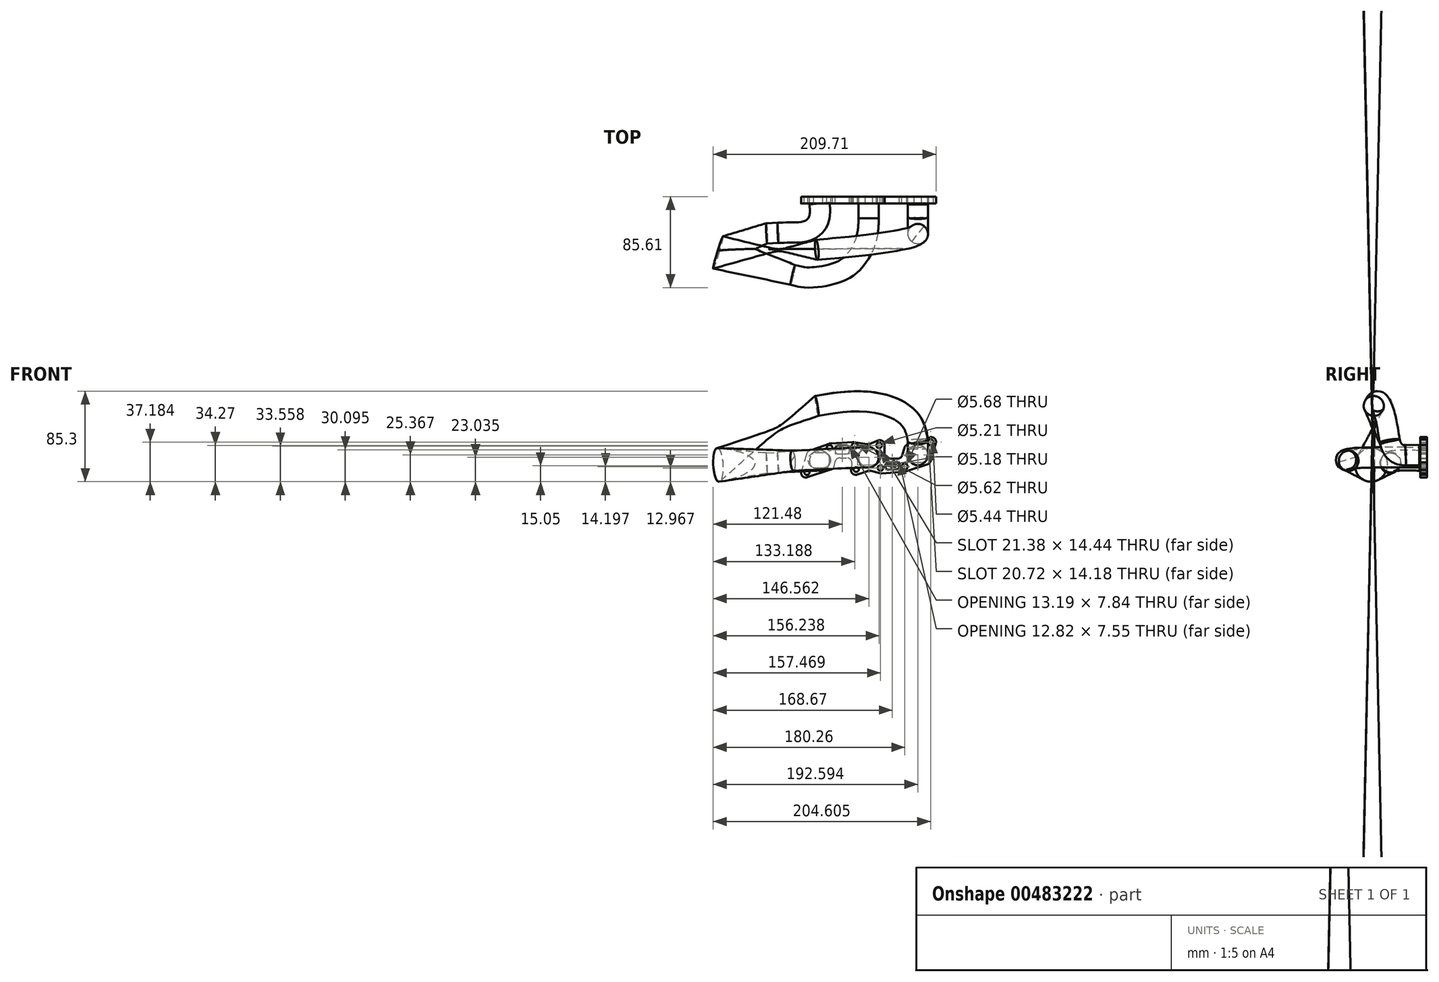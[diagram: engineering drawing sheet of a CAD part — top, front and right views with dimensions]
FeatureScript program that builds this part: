
annotation { "Feature Type Name" : "Feature", "Feature Type Description" : "" }
export const myFeature = defineFeature(function(context is Context, id is Id, definition is map)
    precondition{}
    {
        {
            var Q0;
            Q0=qCreatedBy(makeId("Front.planeOp"),FACE);
            var sketch = newSketch(context, id + "F0", { "sketchPlane" : qUnion([Q0])});
            skLineSegment(sketch, "E0", {"start": v(-73.48, -2.45) * mm, "end": v(-78.33, -18.68) * mm});
            skLineSegment(sketch, "E1", {"start": v(-72.7, -24.18) * mm, "end": v(-50.65, -16.95) * mm});
            skLineSegment(sketch, "E2", {"start": v(-47.2, -12.82) * mm, "end": v(-46.84, -10.23) * mm});
            skLineSegment(sketch, "E3", {"start": v(-41.8, -5.85) * mm, "end": v(-35.77, -5.85) * mm});
            skLineSegment(sketch, "E4", {"start": v(-30.75, -11.68) * mm, "end": v(-31.51, -16.81) * mm});
            skLineSegment(sketch, "E5", {"start": v(-25.64, -21.66) * mm, "end": v(-16.08, -18.29) * mm});
            skLineSegment(sketch, "E6", {"start": v(-13.09, -18.17) * mm, "end": v(-4.67, -20.4) * mm});
            skLineSegment(sketch, "E7", {"start": v(-3, -20.56) * mm, "end": v(18.71, -18.98) * mm});
            skLineSegment(sketch, "E8", {"start": v(19.92, -18.74) * mm, "end": v(40.2, -12.13) * mm});
            skLineSegment(sketch, "E9", {"start": v(43.5, -8.7) * mm, "end": v(48.23, 7.92) * mm});
            skLineSegment(sketch, "E10", {"start": v(42.6, 13.37) * mm, "end": v(21.88, 6.74) * mm});
            skLineSegment(sketch, "E11", {"start": v(18.52, 3.22) * mm, "end": v(16.86, -2.97) * mm});
            skLineSegment(sketch, "E12", {"start": v(11.95, -6.74) * mm, "end": v(5.08, -6.74) * mm});
            skLineSegment(sketch, "E13", {"start": v(0, -1.66) * mm, "end": v(0, 6.27) * mm});
            skLineSegment(sketch, "E14", {"start": v(-6.09, 10.4) * mm, "end": v(-13.83, 7.32) * mm});
            skLineSegment(sketch, "E15", {"start": v(-16.46, 7.02) * mm, "end": v(-28.88, 8.87) * mm});
            skLineSegment(sketch, "E16", {"start": v(-29.9, 8.92) * mm, "end": v(-50.7, 7.78) * mm});
            skLineSegment(sketch, "E17", {"start": v(-52.15, 7.48) * mm, "end": v(-70.34, 0.87) * mm});
            skLineSegment(sketch, "E18", {"start": v(-64.86, -0.9) * mm, "end": v(-57.65, -0.9) * mm});
            skLineSegment(sketch, "E19", {"start": v(-66.6, -15.1) * mm, "end": v(-58.23, -15.1) * mm});
            skArc(sketch, "E20", {"start": v(-64.86, -0.9) * mm, "mid": v(-72, -7.23) * mm, "end": v(-66.6, -15.1) * mm});
            skArc(sketch, "E21", {"start": v(-57.65, -0.9) * mm, "mid": v(-50.55, -8.3) * mm, "end": v(-58.23, -15.1) * mm});
            skLineSegment(sketch, "E22", {"start": v(-43.8, -2.2) * mm, "end": v(-35.78, -2.2) * mm});
            skLineSegment(sketch, "E23", {"start": v(-33.24, 0.34) * mm, "end": v(-33.24, 3.1) * mm});
            skLineSegment(sketch, "E24", {"start": v(-35.78, 5.63) * mm, "end": v(-43.88, 5.63) * mm});
            skLineSegment(sketch, "E25", {"start": v(-46.42, 3) * mm, "end": v(-46.33, 0.25) * mm});
            skLineSegment(sketch, "E26", {"start": v(-18.09, -12.57) * mm, "end": v(-11.17, -12.34) * mm});
            skLineSegment(sketch, "E27", {"start": v(-18.22, 1.88) * mm, "end": v(-11.17, 1.88) * mm});
            skArc(sketch, "E28", {"start": v(-18.22, 1.88) * mm, "mid": v(-25.44, -5.4) * mm, "end": v(-18.09, -12.57) * mm});
            skArc(sketch, "E29", {"start": v(-11.17, 1.88) * mm, "mid": v(-4.06, -5.23) * mm, "end": v(-11.17, -12.34) * mm});
            skLineSegment(sketch, "E30", {"start": v(27.76, -10.1) * mm, "end": v(34.68, -10.1) * mm});
            skLineSegment(sketch, "E31", {"start": v(28.01, 4.08) * mm, "end": v(34.55, 4.08) * mm});
            skArc(sketch, "E32", {"start": v(28.01, 4.08) * mm, "mid": v(20.92, -2.89) * mm, "end": v(27.76, -10.1) * mm});
            skArc(sketch, "E33", {"start": v(34.55, 4.08) * mm, "mid": v(41.64, -2.95) * mm, "end": v(34.68, -10.1) * mm});
            skLineSegment(sketch, "E34", {"start": v(3.6, -17.1) * mm, "end": v(11.35, -16.75) * mm});
            skLineSegment(sketch, "E35", {"start": v(13.77, -14.22) * mm, "end": v(13.77, -12.09) * mm});
            skLineSegment(sketch, "E36", {"start": v(11.08, -9.55) * mm, "end": v(3.34, -10.02) * mm});
            skLineSegment(sketch, "E37", {"start": v(0.95, -12.56) * mm, "end": v(0.95, -14.57) * mm});
            skCircle(sketch, "E38", {"center": v(-73.06, -19.56) * mm, "radius": 2.44 * mm});
            skCircle(sketch, "E39", {"center": v(-51.69, 3.62) * mm, "radius": 2.58 * mm});
            skCircle(sketch, "E40", {"center": v(-28.12, 5.18) * mm, "radius": 2.8 * mm});
            skCircle(sketch, "E41", {"center": v(-26.7, -16.7) * mm, "radius": 2.47 * mm});
            skCircle(sketch, "E42", {"center": v(-3.84, -15.41) * mm, "radius": 2.6 * mm});
            skCircle(sketch, "E43", {"center": v(-5.07, 5.9) * mm, "radius": 2.6 * mm});
            skCircle(sketch, "E44", {"center": v(18.95, -14.18) * mm, "radius": 2.84 * mm});
            skCircle(sketch, "E45", {"center": v(43.3, 8.8) * mm, "radius": 2.72 * mm});
            skPoint(sketch, "E46.visualSharp", {"position": v(50.5, 15.9) * mm});
            skArc(sketch, "E46.filletArc", {"start": v(48.23, 7.92) * mm, "mid": v(47.05, 12.33) * mm, "end": v(42.6, 13.37) * mm});
            skPoint(sketch, "E47.visualSharp", {"position": v(0, 12.82) * mm});
            skArc(sketch, "E47.filletArc", {"start": v(0, 6.27) * mm, "mid": v(-1.95, 9.95) * mm, "end": v(-6.09, 10.4) * mm});
            skPoint(sketch, "E48.visualSharp", {"position": v(-32.6, -24.11) * mm});
            skArc(sketch, "E48.filletArc", {"start": v(-31.51, -16.81) * mm, "mid": v(-29.95, -20.9) * mm, "end": v(-25.64, -21.66) * mm});
            skPoint(sketch, "E49.visualSharp", {"position": v(-80.77, -26.83) * mm});
            skArc(sketch, "E49.filletArc", {"start": v(-78.33, -18.68) * mm, "mid": v(-77.18, -23.14) * mm, "end": v(-72.7, -24.18) * mm});
            skPoint(sketch, "E50.visualSharp", {"position": v(-47.63, -15.96) * mm});
            skArc(sketch, "E50.filletArc", {"start": v(-50.65, -16.95) * mm, "mid": v(-48.33, -15.38) * mm, "end": v(-47.2, -12.82) * mm});
            skPoint(sketch, "E51.visualSharp", {"position": v(-46.23, -5.85) * mm});
            skArc(sketch, "E51.filletArc", {"start": v(-41.8, -5.85) * mm, "mid": v(-45.14, -7.1) * mm, "end": v(-46.84, -10.23) * mm});
            skPoint(sketch, "E52.visualSharp", {"position": v(-29.88, -5.85) * mm});
            skArc(sketch, "E52.filletArc", {"start": v(-30.75, -11.68) * mm, "mid": v(-31.93, -7.62) * mm, "end": v(-35.77, -5.85) * mm});
            skPoint(sketch, "E53.visualSharp", {"position": v(-14.6, -17.77) * mm});
            skArc(sketch, "E53.filletArc", {"start": v(-13.09, -18.17) * mm, "mid": v(-14.6, -18) * mm, "end": v(-16.08, -18.29) * mm});
            skPoint(sketch, "E54.visualSharp", {"position": v(-3.85, -20.62) * mm});
            skArc(sketch, "E54.filletArc", {"start": v(-4.67, -20.4) * mm, "mid": v(-3.84, -20.55) * mm, "end": v(-3, -20.56) * mm});
            skPoint(sketch, "E55.visualSharp", {"position": v(19.33, -18.93) * mm});
            skArc(sketch, "E55.filletArc", {"start": v(18.71, -18.98) * mm, "mid": v(19.32, -18.9) * mm, "end": v(19.92, -18.74) * mm});
            skPoint(sketch, "E56.visualSharp", {"position": v(42.77, -11.3) * mm});
            skArc(sketch, "E56.filletArc", {"start": v(40.2, -12.13) * mm, "mid": v(42.28, -10.83) * mm, "end": v(43.5, -8.7) * mm});
            skPoint(sketch, "E57.visualSharp", {"position": v(19.24, 5.9) * mm});
            skArc(sketch, "E57.filletArc", {"start": v(21.88, 6.74) * mm, "mid": v(19.75, 5.4) * mm, "end": v(18.52, 3.22) * mm});
            skPoint(sketch, "E58.visualSharp", {"position": v(15.85, -6.74) * mm});
            skArc(sketch, "E58.filletArc", {"start": v(11.95, -6.74) * mm, "mid": v(15.05, -5.69) * mm, "end": v(16.86, -2.97) * mm});
            skPoint(sketch, "E59.visualSharp", {"position": v(0, -6.74) * mm});
            skArc(sketch, "E59.filletArc", {"start": v(0, -1.66) * mm, "mid": v(1.49, -5.25) * mm, "end": v(5.08, -6.74) * mm});
            skPoint(sketch, "E60.visualSharp", {"position": v(-72.74, 0) * mm});
            skArc(sketch, "E60.filletArc", {"start": v(-70.34, 0.87) * mm, "mid": v(-72.3, -0.42) * mm, "end": v(-73.48, -2.45) * mm});
            skPoint(sketch, "E61.visualSharp", {"position": v(-51.44, 7.74) * mm});
            skArc(sketch, "E61.filletArc", {"start": v(-50.7, 7.78) * mm, "mid": v(-51.43, 7.69) * mm, "end": v(-52.15, 7.48) * mm});
            skPoint(sketch, "E62.visualSharp", {"position": v(-29.39, 8.94) * mm});
            skArc(sketch, "E62.filletArc", {"start": v(-28.88, 8.87) * mm, "mid": v(-29.39, 8.92) * mm, "end": v(-29.9, 8.92) * mm});
            skPoint(sketch, "E63.visualSharp", {"position": v(-15.1, 6.82) * mm});
            skArc(sketch, "E63.filletArc", {"start": v(-16.46, 7.02) * mm, "mid": v(-15.12, 7) * mm, "end": v(-13.83, 7.32) * mm});
            skPoint(sketch, "E64.visualSharp", {"position": v(-46.25, -2.2) * mm});
            skArc(sketch, "E64.filletArc", {"start": v(-46.33, 0.25) * mm, "mid": v(-45.56, -1.49) * mm, "end": v(-43.8, -2.2) * mm});
            skPoint(sketch, "E65.visualSharp", {"position": v(-33.24, -2.2) * mm});
            skArc(sketch, "E65.filletArc", {"start": v(-35.78, -2.2) * mm, "mid": v(-33.98, -1.46) * mm, "end": v(-33.24, 0.34) * mm});
            skPoint(sketch, "E66.visualSharp", {"position": v(-33.24, 5.63) * mm});
            skArc(sketch, "E66.filletArc", {"start": v(-33.24, 3.1) * mm, "mid": v(-33.98, 4.89) * mm, "end": v(-35.78, 5.63) * mm});
            skPoint(sketch, "E67.visualSharp", {"position": v(-46.51, 5.63) * mm});
            skArc(sketch, "E67.filletArc", {"start": v(-43.88, 5.63) * mm, "mid": v(-45.71, 4.86) * mm, "end": v(-46.42, 3) * mm});
            skPoint(sketch, "E68.visualSharp", {"position": v(0.95, -10.17) * mm});
            skArc(sketch, "E68.filletArc", {"start": v(3.34, -10.02) * mm, "mid": v(1.64, -10.82) * mm, "end": v(0.95, -12.56) * mm});
            skPoint(sketch, "E69.visualSharp", {"position": v(13.77, -9.4) * mm});
            skArc(sketch, "E69.filletArc", {"start": v(13.77, -12.09) * mm, "mid": v(12.97, -10.24) * mm, "end": v(11.08, -9.55) * mm});
            skPoint(sketch, "E70.visualSharp", {"position": v(13.77, -16.64) * mm});
            skArc(sketch, "E70.filletArc", {"start": v(11.35, -16.75) * mm, "mid": v(13.07, -15.97) * mm, "end": v(13.77, -14.22) * mm});
            skPoint(sketch, "E71.visualSharp", {"position": v(0.95, -17.23) * mm});
            skArc(sketch, "E71.filletArc", {"start": v(0.95, -14.57) * mm, "mid": v(1.73, -16.4) * mm, "end": v(3.6, -17.1) * mm});
            skPoint(sketch, "E72", {"position": v(-61.27, -8.01) * mm});
            skPoint(sketch, "E73", {"position": v(-14.89, -5.4) * mm});
            skPoint(sketch, "E73.positionSnap0", {"position": v(-25.44, -5.4) * mm});
            skPoint(sketch, "E74", {"position": v(31.4, -3.13) * mm});
            skSolve(sketch);
        }
        {
            var Q0;
            Q0=makeQuery(id+"F0.imprint","IMPRINT",FACE,{"disambiguationData":[TD([[makeQuery(id+"F0.imprint","IMPRINT",EDGE,{"derivedFrom":sQuery(id+"F0.wireOp",EDGE,"E0")}),1.0]])]});
            extrude(context, id + "F1", {"entities" : qUnion([Q0]), "depth" : 6.35 * mm});
        }
        {
            var Q0;
            Q0=qCreatedBy(makeId("Right.planeOp"),FACE);
            cPlane(context, id + "F2", {"entities" : qUnion([Q0]), "cplaneType" : CPlaneType.OFFSET, "offset" : 61.2 * mm, "oppositeDirection" : true, "width" : 152.4 * mm, "height" : 152.4 * mm});
        }
        {
            var Q0;
            Q0=qCreatedBy(id+"F2.planeOp",FACE);
            cPlane(context, id + "F3", {"entities" : qUnion([Q0]), "cplaneType" : CPlaneType.OFFSET, "offset" : 46.23 * mm, "width" : 152.4 * mm, "height" : 152.4 * mm});
        }
        {
            var Q0;
            Q0=qCreatedBy(id+"F2.planeOp",FACE);
            cPlane(context, id + "F4", {"entities" : qUnion([Q0]), "cplaneType" : CPlaneType.OFFSET, "offset" : 92.66 * mm, "width" : 152.4 * mm, "height" : 152.4 * mm});
        }
        {
            var Q0;
            Q0=makeQuery(id+"F1.opExtrude","CAP_FACE",FACE,{"disambiguationData":[OSD([sQuery(id+"F0.wireOp",EDGE,"E0"),sQuery(id+"F0.wireOp",EDGE,"E1"),sQuery(id+"F0.wireOp",EDGE,"E2"),sQuery(id+"F0.wireOp",EDGE,"E3"),sQuery(id+"F0.wireOp",EDGE,"E4"),sQuery(id+"F0.wireOp",EDGE,"E5"),sQuery(id+"F0.wireOp",EDGE,"E6"),sQuery(id+"F0.wireOp",EDGE,"E7"),sQuery(id+"F0.wireOp",EDGE,"E8"),sQuery(id+"F0.wireOp",EDGE,"E9"),sQuery(id+"F0.wireOp",EDGE,"E10"),sQuery(id+"F0.wireOp",EDGE,"E11"),sQuery(id+"F0.wireOp",EDGE,"E12"),sQuery(id+"F0.wireOp",EDGE,"E13"),sQuery(id+"F0.wireOp",EDGE,"E14"),sQuery(id+"F0.wireOp",EDGE,"E15"),sQuery(id+"F0.wireOp",EDGE,"E16"),sQuery(id+"F0.wireOp",EDGE,"E17"),sQuery(id+"F0.wireOp",EDGE,"E18"),sQuery(id+"F0.wireOp",EDGE,"E19"),sQuery(id+"F0.wireOp",EDGE,"E20"),sQuery(id+"F0.wireOp",EDGE,"E21"),sQuery(id+"F0.wireOp",EDGE,"E22"),sQuery(id+"F0.wireOp",EDGE,"E23"),sQuery(id+"F0.wireOp",EDGE,"E24"),sQuery(id+"F0.wireOp",EDGE,"E25"),sQuery(id+"F0.wireOp",EDGE,"E26"),sQuery(id+"F0.wireOp",EDGE,"E27"),sQuery(id+"F0.wireOp",EDGE,"E28"),sQuery(id+"F0.wireOp",EDGE,"E29"),sQuery(id+"F0.wireOp",EDGE,"E30"),sQuery(id+"F0.wireOp",EDGE,"E31"),sQuery(id+"F0.wireOp",EDGE,"E32"),sQuery(id+"F0.wireOp",EDGE,"E33"),sQuery(id+"F0.wireOp",EDGE,"E34"),sQuery(id+"F0.wireOp",EDGE,"E35"),sQuery(id+"F0.wireOp",EDGE,"E36"),sQuery(id+"F0.wireOp",EDGE,"E37"),sQuery(id+"F0.wireOp",EDGE,"E38"),sQuery(id+"F0.wireOp",EDGE,"E39"),sQuery(id+"F0.wireOp",EDGE,"E40"),sQuery(id+"F0.wireOp",EDGE,"E41"),sQuery(id+"F0.wireOp",EDGE,"E42"),sQuery(id+"F0.wireOp",EDGE,"E43"),sQuery(id+"F0.wireOp",EDGE,"E44"),sQuery(id+"F0.wireOp",EDGE,"E45"),sQuery(id+"F0.wireOp",EDGE,"E46.filletArc"),sQuery(id+"F0.wireOp",EDGE,"E47.filletArc"),sQuery(id+"F0.wireOp",EDGE,"E48.filletArc"),sQuery(id+"F0.wireOp",EDGE,"E49.filletArc"),sQuery(id+"F0.wireOp",EDGE,"E50.filletArc"),sQuery(id+"F0.wireOp",EDGE,"E51.filletArc"),sQuery(id+"F0.wireOp",EDGE,"E52.filletArc"),sQuery(id+"F0.wireOp",EDGE,"E53.filletArc"),sQuery(id+"F0.wireOp",EDGE,"E54.filletArc"),sQuery(id+"F0.wireOp",EDGE,"E55.filletArc"),sQuery(id+"F0.wireOp",EDGE,"E56.filletArc"),sQuery(id+"F0.wireOp",EDGE,"E57.filletArc"),sQuery(id+"F0.wireOp",EDGE,"E58.filletArc"),sQuery(id+"F0.wireOp",EDGE,"E59.filletArc"),sQuery(id+"F0.wireOp",EDGE,"E60.filletArc"),sQuery(id+"F0.wireOp",EDGE,"E61.filletArc"),sQuery(id+"F0.wireOp",EDGE,"E62.filletArc"),sQuery(id+"F0.wireOp",EDGE,"E63.filletArc"),sQuery(id+"F0.wireOp",EDGE,"E64.filletArc"),sQuery(id+"F0.wireOp",EDGE,"E65.filletArc"),sQuery(id+"F0.wireOp",EDGE,"E66.filletArc"),sQuery(id+"F0.wireOp",EDGE,"E67.filletArc"),sQuery(id+"F0.wireOp",EDGE,"E68.filletArc"),sQuery(id+"F0.wireOp",EDGE,"E69.filletArc"),sQuery(id+"F0.wireOp",EDGE,"E70.filletArc"),sQuery(id+"F0.wireOp",EDGE,"E71.filletArc")])],"isStart":false});
            cPlane(context, id + "F5", {"entities" : qUnion([Q0]), "cplaneType" : CPlaneType.OFFSET, "offset" : 0 * mm, "width" : 152.4 * mm, "height" : 152.4 * mm});
        }
        {
            var Q0;
            Q0=qCreatedBy(id+"F5.planeOp",FACE);
            var sketch = newSketch(context, id + "F6", { "sketchPlane" : qUnion([Q0])});
            skPoint(sketch, "E75", {"position": v(-61.33, -8.01) * mm});
            skPoint(sketch, "E76", {"position": v(-14.86, -5.46) * mm});
            skPoint(sketch, "E77", {"position": v(31.4, -3.17) * mm});
            skSolve(sketch);
        }
        {
            var Q0;
            Q0=qCreatedBy(id+"F3.planeOp",FACE);
            var sketch = newSketch(context, id + "F7", { "sketchPlane" : qUnion([Q0])});
            skLineSegment(sketch, "E78", {"start": v(-6.35, -5.46) * mm, "end": v(-20.21, -5.46) * mm});
            skPoint(sketch, "E79", {"position": v(-6.35, -5.46) * mm});
            skSolve(sketch);
        }
        {
            var Q0;
            Q0=makeQuery(id+"F1.opExtrude","CAP_FACE",FACE,{"disambiguationData":[OSD([sQuery(id+"F0.wireOp",EDGE,"E0"),sQuery(id+"F0.wireOp",EDGE,"E1"),sQuery(id+"F0.wireOp",EDGE,"E2"),sQuery(id+"F0.wireOp",EDGE,"E3"),sQuery(id+"F0.wireOp",EDGE,"E4"),sQuery(id+"F0.wireOp",EDGE,"E5"),sQuery(id+"F0.wireOp",EDGE,"E6"),sQuery(id+"F0.wireOp",EDGE,"E7"),sQuery(id+"F0.wireOp",EDGE,"E8"),sQuery(id+"F0.wireOp",EDGE,"E9"),sQuery(id+"F0.wireOp",EDGE,"E10"),sQuery(id+"F0.wireOp",EDGE,"E11"),sQuery(id+"F0.wireOp",EDGE,"E12"),sQuery(id+"F0.wireOp",EDGE,"E13"),sQuery(id+"F0.wireOp",EDGE,"E14"),sQuery(id+"F0.wireOp",EDGE,"E15"),sQuery(id+"F0.wireOp",EDGE,"E16"),sQuery(id+"F0.wireOp",EDGE,"E17"),sQuery(id+"F0.wireOp",EDGE,"E18"),sQuery(id+"F0.wireOp",EDGE,"E19"),sQuery(id+"F0.wireOp",EDGE,"E20"),sQuery(id+"F0.wireOp",EDGE,"E21"),sQuery(id+"F0.wireOp",EDGE,"E22"),sQuery(id+"F0.wireOp",EDGE,"E23"),sQuery(id+"F0.wireOp",EDGE,"E24"),sQuery(id+"F0.wireOp",EDGE,"E25"),sQuery(id+"F0.wireOp",EDGE,"E26"),sQuery(id+"F0.wireOp",EDGE,"E27"),sQuery(id+"F0.wireOp",EDGE,"E28"),sQuery(id+"F0.wireOp",EDGE,"E29"),sQuery(id+"F0.wireOp",EDGE,"E30"),sQuery(id+"F0.wireOp",EDGE,"E31"),sQuery(id+"F0.wireOp",EDGE,"E32"),sQuery(id+"F0.wireOp",EDGE,"E33"),sQuery(id+"F0.wireOp",EDGE,"E34"),sQuery(id+"F0.wireOp",EDGE,"E35"),sQuery(id+"F0.wireOp",EDGE,"E36"),sQuery(id+"F0.wireOp",EDGE,"E37"),sQuery(id+"F0.wireOp",EDGE,"E38"),sQuery(id+"F0.wireOp",EDGE,"E39"),sQuery(id+"F0.wireOp",EDGE,"E40"),sQuery(id+"F0.wireOp",EDGE,"E41"),sQuery(id+"F0.wireOp",EDGE,"E42"),sQuery(id+"F0.wireOp",EDGE,"E43"),sQuery(id+"F0.wireOp",EDGE,"E44"),sQuery(id+"F0.wireOp",EDGE,"E45"),sQuery(id+"F0.wireOp",EDGE,"E46.filletArc"),sQuery(id+"F0.wireOp",EDGE,"E47.filletArc"),sQuery(id+"F0.wireOp",EDGE,"E48.filletArc"),sQuery(id+"F0.wireOp",EDGE,"E49.filletArc"),sQuery(id+"F0.wireOp",EDGE,"E50.filletArc"),sQuery(id+"F0.wireOp",EDGE,"E51.filletArc"),sQuery(id+"F0.wireOp",EDGE,"E52.filletArc"),sQuery(id+"F0.wireOp",EDGE,"E53.filletArc"),sQuery(id+"F0.wireOp",EDGE,"E54.filletArc"),sQuery(id+"F0.wireOp",EDGE,"E55.filletArc"),sQuery(id+"F0.wireOp",EDGE,"E56.filletArc"),sQuery(id+"F0.wireOp",EDGE,"E57.filletArc"),sQuery(id+"F0.wireOp",EDGE,"E58.filletArc"),sQuery(id+"F0.wireOp",EDGE,"E59.filletArc"),sQuery(id+"F0.wireOp",EDGE,"E60.filletArc"),sQuery(id+"F0.wireOp",EDGE,"E61.filletArc"),sQuery(id+"F0.wireOp",EDGE,"E62.filletArc"),sQuery(id+"F0.wireOp",EDGE,"E63.filletArc"),sQuery(id+"F0.wireOp",EDGE,"E64.filletArc"),sQuery(id+"F0.wireOp",EDGE,"E65.filletArc"),sQuery(id+"F0.wireOp",EDGE,"E66.filletArc"),sQuery(id+"F0.wireOp",EDGE,"E67.filletArc"),sQuery(id+"F0.wireOp",EDGE,"E68.filletArc"),sQuery(id+"F0.wireOp",EDGE,"E69.filletArc"),sQuery(id+"F0.wireOp",EDGE,"E70.filletArc"),sQuery(id+"F0.wireOp",EDGE,"E71.filletArc")])],"isStart":false});
            cPlane(context, id + "F8", {"entities" : qUnion([Q0]), "cplaneType" : CPlaneType.OFFSET, "offset" : 13.9 * mm, "width" : 152.4 * mm, "height" : 152.4 * mm});
        }
        {
            var Q0;
            Q0=qCreatedBy(id+"F8.planeOp",FACE);
            var sketch = newSketch(context, id + "F9", { "sketchPlane" : qUnion([Q0])});
            skCircle(sketch, "E80", {"center": v(-14.99, -5.46) * mm, "radius": 9.53 * mm});
            skCircle(sketch, "E81", {"center": v(-61.43, -8.06) * mm, "radius": 9.53 * mm});
            skCircle(sketch, "E82", {"center": v(31.33, -3.18) * mm, "radius": 9.53 * mm});
            skSolve(sketch);
        }
        {
            var Q0;
            Q0=sQuery(id+"F6.wireOp",VERTEX,"E75");
            var Q1;
            Q1=sQuery(id+"F6.wireOp",VERTEX,"E77");
            var Q2;
            Q2=sQuery(id+"F9.wireOp",VERTEX,"E80.center");
            cPlane(context, id + "F10", {"entities" : qUnion([Q0, Q1, Q2]), "cplaneType" : CPlaneType.THREE_POINT, "offset" : 5.46 * mm, "oppositeDirection" : true, "width" : 152.4 * mm, "height" : 152.4 * mm});
        }
        {
            var Q0;
            Q0=qCreatedBy(id+"F10.planeOp",FACE);
            var sketch = newSketch(context, id + "F11", { "sketchPlane" : qUnion([Q0])});
            skPoint(sketch, "E83", {"position": v(-61.66, -6.27) * mm});
            skPoint(sketch, "E84", {"position": v(-15.28, -20.2) * mm});
            skPoint(sketch, "E85", {"position": v(31.2, -6.32) * mm});
            skFitSpline(sketch, "E86", {"points": [v(-61.66, -6.27) * mm, v(-61.66, -18.76) * mm, v(-66.36, -27.74) * mm, v(-76.04, -32.67) * mm, v(-89.72, -33.53) * mm, v(-100.53, -33.78) * mm], "startDerivative": vector(5.23, -58.12) * mm, "endDerivative": vector(-29.2, -0.3) * mm});
            skLineSegment(sketch, "E87", {"start": v(-100.53, -33.78) * mm, "end": v(-111.3, -34.25) * mm});
            skLineSegment(sketch, "E88", {"start": v(-111.3, -34.25) * mm, "end": v(-157.14, -52.33) * mm});
            skFitSpline(sketch, "E89", {"points": [v(-15.28, -20.2) * mm, v(-17.12, -38.06) * mm, v(-24.15, -54.37) * mm, v(-40.79, -69.62) * mm, v(-72.94, -75.97) * mm, v(-86.74, -73.5) * mm], "startDerivative": vector(0.24, -95.26) * mm, "endDerivative": vector(-96.92, 22.9) * mm});
            skLineSegment(sketch, "E90", {"start": v(-86.74, -73.5) * mm, "end": v(-157.14, -52.33) * mm});
            skLineSegment(sketch, "E91", {"start": v(31.2, -6.32) * mm, "end": v(31.2, -19.28) * mm});
            skSolve(sketch);
        }
        {
            var Q0;
            Q0=qCreatedBy(id+"F4.planeOp",FACE);
            var sketch = newSketch(context, id + "F12", { "sketchPlane" : qUnion([Q0])});
            skFitSpline(sketch, "E92", {"points": [v(-19.3, -3.04) * mm, v(-25.94, -2.52) * mm, v(-29.93, 0) * mm, v(-34.92, 9.76) * mm], "startDerivative": vector(-28.04, -4.68) * mm, "endDerivative": vector(-11.55, 40.68) * mm});
            skSolve(sketch);
        }
        {
            var Q0;
            Q0=sQuery(id+"F11.wireOp",VERTEX,"E90.end");
            var Q1;
            Q1=sQuery(id+"F12.wireOp",VERTEX,"E92.end");
            var Q2;
            Q2=sQuery(id+"F11.wireOp",VERTEX,"E89.1.internal");
            cPlane(context, id + "F13", {"entities" : qUnion([Q0, Q1, Q2]), "cplaneType" : CPlaneType.THREE_POINT, "offset" : 25.4 * mm, "width" : 152.4 * mm, "height" : 152.4 * mm});
        }
        {
            var Q0;
            Q0=qCreatedBy(id+"F13.planeOp",FACE);
            var sketch = newSketch(context, id + "F14", { "sketchPlane" : qUnion([Q0])});
            skPoint(sketch, "E93", {"position": v(27.67, 14.49) * mm});
            skPoint(sketch, "E94", {"position": v(-161.55, -5.2) * mm});
            skFitSpline(sketch, "E95", {"points": [v(27.67, 14.49) * mm, v(23.4, 30.16) * mm, v(8.38, 44.59) * mm, v(-26.57, 53.23) * mm, v(-68.16, 49.5) * mm], "startDerivative": vector(-13.52, 84.18) * mm, "endDerivative": vector(-135.67, -21.3) * mm});
            skLineSegment(sketch, "E96", {"start": v(-161.55, -5.2) * mm, "end": v(-68.16, 49.5) * mm});
            skSolve(sketch);
        }
        {
            var Q0;
            Q0=sQuery(id+"F11.wireOp",VERTEX,"E89.1.internal");
            var Q1;
            Q1=sQuery(id+"F11.wireOp",EDGE,"E89");
            cPlane(context, id + "F15", {"entities" : qUnion([Q0, Q1]), "cplaneType" : CPlaneType.CURVE_POINT, "offset" : 25.4 * mm, "width" : 152.4 * mm, "height" : 152.4 * mm});
        }
        {
            var Q0;
            Q0=sQuery(id+"F11.wireOp",VERTEX,"E89.2.internal");
            var Q1;
            Q1=sQuery(id+"F11.wireOp",EDGE,"E89");
            cPlane(context, id + "F16", {"entities" : qUnion([Q0, Q1]), "cplaneType" : CPlaneType.CURVE_POINT, "offset" : 25.4 * mm, "width" : 152.4 * mm, "height" : 152.4 * mm});
        }
        {
            var Q0;
            Q0=sQuery(id+"F11.wireOp",VERTEX,"E89.3.internal");
            var Q1;
            Q1=sQuery(id+"F11.wireOp",EDGE,"E89");
            cPlane(context, id + "F17", {"entities" : qUnion([Q0, Q1]), "cplaneType" : CPlaneType.CURVE_POINT, "offset" : 25.4 * mm, "width" : 152.4 * mm, "height" : 152.4 * mm});
        }
        {
            var Q0;
            Q0=sQuery(id+"F11.wireOp",VERTEX,"E89.4.internal");
            var Q1;
            Q1=sQuery(id+"F11.wireOp",EDGE,"E89");
            cPlane(context, id + "F18", {"entities" : qUnion([Q0, Q1]), "cplaneType" : CPlaneType.CURVE_POINT, "offset" : 25.4 * mm, "width" : 152.4 * mm, "height" : 152.4 * mm});
        }
        {
            var Q0;
            Q0=sQuery(id+"F11.wireOp",VERTEX,"E90.start");
            var Q1;
            Q1=sQuery(id+"F11.wireOp",EDGE,"E89");
            cPlane(context, id + "F19", {"entities" : qUnion([Q0, Q1]), "cplaneType" : CPlaneType.CURVE_POINT, "offset" : 25.4 * mm, "width" : 152.4 * mm, "height" : 152.4 * mm});
        }
        {
            var Q0;
            Q0=qCreatedBy(id+"F19.planeOp",FACE);
            var sketch = newSketch(context, id + "F20", { "sketchPlane" : qUnion([Q0])});
            skPoint(sketch, "E97", {"position": v(91.51, -3.93) * mm});
            skCircle(sketch, "E98", {"center": v(91.51, -3.93) * mm, "radius": 9.53 * mm});
            skSolve(sketch);
        }
        {
            var Q0;
            Q0=sQuery(id+"F14.wireOp",VERTEX,"E94");
            var Q1;
            Q1=sQuery(id+"F11.wireOp",EDGE,"E90");
            cPlane(context, id + "F21", {"entities" : qUnion([Q0, Q1]), "cplaneType" : CPlaneType.LINE_POINT, "offset" : 25.4 * mm, "width" : 152.4 * mm, "height" : 152.4 * mm});
        }
        {
            var Q0;
            Q0=qCreatedBy(id+"F21.planeOp",FACE);
            var sketch = newSketch(context, id + "F22", { "sketchPlane" : qUnion([Q0])});
            skPoint(sketch, "E99", {"position": v(95.39, -3.87) * mm});
            skCircle(sketch, "E100", {"center": v(95.39, -3.87) * mm, "radius": 15.88 * mm});
            skSolve(sketch);
        }
        {
            var Q0;
            Q0=makeQuery(id+"F9.imprint","IMPRINT",FACE,{"disambiguationData":[TD([[makeQuery(id+"F9.imprint","IMPRINT",EDGE,{"derivedFrom":sQuery(id+"F9.wireOp",EDGE,"E80")}),1.0]])]});
            var Q1;
            Q1=sQuery(id+"F7.wireOp",EDGE,"E78");
            sweep(context, id + "F23", {"profiles" : qUnion([Q0]), "path" : qUnion([Q1])});
        }
        {
            var Q0;
            Q0=makeQuery(id+"F9.imprint","IMPRINT",FACE,{"disambiguationData":[TD([[makeQuery(id+"F9.imprint","IMPRINT",EDGE,{"derivedFrom":sQuery(id+"F9.wireOp",EDGE,"E80")}),1.0]])]});
            var Q1;
            Q1=sQuery(id+"F11.wireOp",EDGE,"E89");
            sweep(context, id + "F24", {"operationType" : NewBodyOperationType.ADD, "profiles" : qUnion([Q0]), "path" : qUnion([Q1])});
        }
        {
            var Q1;
            Q1=makeQuery(id+"F22.imprint","IMPRINT",FACE,{"disambiguationData":[TD([[makeQuery(id+"F22.imprint","IMPRINT",EDGE,{"derivedFrom":sQuery(id+"F22.wireOp",EDGE,"E100")}),1.0]])]});
            var Q2;
            Q2=makeQuery(id+"F20.imprint","IMPRINT",FACE,{"disambiguationData":[TD([[makeQuery(id+"F20.imprint","IMPRINT",EDGE,{"derivedFrom":sQuery(id+"F20.wireOp",EDGE,"E98")}),1.0]])]});
            loft(context, id + "F25", {"operationType" : NewBodyOperationType.ADD, "sheetProfilesArray" : [{ "sheetProfileEntities" : qUnion([Q1]) }, { "sheetProfileEntities" : qUnion([Q2]) }]});
        }
        {
            var Q0;
            Q0=sQuery(id+"F11.wireOp",EDGE,"E86");
            cPoint(context, id + "F26", {"entities" : qUnion([Q0]), "parameter" : 0.5});
        }
        {
            var Q0;
            Q0 = qCreatedBy(id + "F26" ,VERTEX);
            var Q1;
            Q1=sQuery(id+"F11.wireOp",EDGE,"E86");
            cPlane(context, id + "F27", {"entities" : qUnion([Q0, Q1]), "cplaneType" : CPlaneType.CURVE_POINT, "offset" : 25.4 * mm, "width" : 152.4 * mm, "height" : 152.4 * mm});
        }
        {
            var Q0;
            Q0=sQuery(id+"F11.wireOp",VERTEX,"E86.3.internal");
            var Q1;
            Q1=sQuery(id+"F11.wireOp",EDGE,"E86");
            cPlane(context, id + "F28", {"entities" : qUnion([Q0, Q1]), "cplaneType" : CPlaneType.CURVE_POINT, "offset" : 25.4 * mm, "width" : 152.4 * mm, "height" : 152.4 * mm});
        }
        {
            var Q0;
            Q0=sQuery(id+"F11.wireOp",VERTEX,"E86.5.internal");
            var Q1;
            Q1=sQuery(id+"F11.wireOp",EDGE,"E86");
            cPlane(context, id + "F29", {"entities" : qUnion([Q0, Q1]), "cplaneType" : CPlaneType.CURVE_POINT, "offset" : 25.4 * mm, "width" : 152.4 * mm, "height" : 152.4 * mm});
        }
        {
            var Q0;
            Q0=sQuery(id+"F11.wireOp",VERTEX,"E88.start");
            var Q1;
            Q1=sQuery(id+"F11.wireOp",EDGE,"E87");
            cPlane(context, id + "F30", {"entities" : qUnion([Q0, Q1]), "cplaneType" : CPlaneType.CURVE_POINT, "offset" : 25.4 * mm, "width" : 152.4 * mm, "height" : 152.4 * mm});
        }
        {
            var Q0;
            Q0=qCreatedBy(id+"F30.planeOp",FACE);
            var sketch = newSketch(context, id + "F31", { "sketchPlane" : qUnion([Q0])});
            skCircle(sketch, "E101", {"center": v(29.5, -5) * mm, "radius": 9.52 * mm});
            skSolve(sketch);
        }
        {
            var Q0;
            Q0=makeQuery(id+"F31.imprint","IMPRINT",FACE,{"disambiguationData":[TD([[makeQuery(id+"F31.imprint","IMPRINT",EDGE,{"derivedFrom":sQuery(id+"F31.wireOp",EDGE,"E101")}),1.0]])]});
            var Q1;
            Q1=sQuery(id+"F11.wireOp",EDGE,"E86");
            var Q2;
            Q2=sQuery(id+"F11.wireOp",EDGE,"E87");
            sweep(context, id + "F32", {"operationType" : NewBodyOperationType.ADD, "profiles" : qUnion([Q0]), "path" : qUnion([Q1, Q2])});
        }
        {
            var Q1;
            Q1=makeQuery(id+"F25.opLoft","CAP_FACE",FACE,{"disambiguationData":[OSD([makeQuery(id+"F22.imprint","IMPRINT",FACE,{"disambiguationData":[TD([[makeQuery(id+"F22.imprint","IMPRINT",EDGE,{"derivedFrom":sQuery(id+"F22.wireOp",EDGE,"E100")}),1.0]])]})])],"isStart":true});
            var Q2;
            Q2=makeQuery(id+"F32.opSweep","CAP_FACE",FACE,{"disambiguationData":[OSD([sQuery(id+"F11.wireOp",VERTEX,"E87.end"),sQuery(id+"F31.wireOp",EDGE,"E101")])],"isStart":true});
            loft(context, id + "F33", {"operationType" : NewBodyOperationType.ADD, "sheetProfilesArray" : [{ "sheetProfileEntities" : qUnion([Q1]) }, { "sheetProfileEntities" : qUnion([Q2]) }]});
        }
        {
            var Q0;
            Q0=sQuery(id+"F12.wireOp",EDGE,"E92");
            cPoint(context, id + "F34", {"entities" : qUnion([Q0]), "parameter" : 0.5});
        }
        {
            var Q0;
            Q0 = qCreatedBy(id + "F34" ,VERTEX);
            var Q1;
            Q1=sQuery(id+"F12.wireOp",EDGE,"E92");
            cPlane(context, id + "F35", {"entities" : qUnion([Q0, Q1]), "cplaneType" : CPlaneType.CURVE_POINT, "offset" : 25.4 * mm, "width" : 152.4 * mm, "height" : 152.4 * mm});
        }
        {
            var Q0;
            Q0=sQuery(id+"F14.wireOp",VERTEX,"E93");
            var Q1;
            Q1=sQuery(id+"F12.wireOp",EDGE,"E92");
            cPlane(context, id + "F36", {"entities" : qUnion([Q0, Q1]), "cplaneType" : CPlaneType.CURVE_POINT, "offset" : 25.4 * mm, "width" : 152.4 * mm, "height" : 152.4 * mm});
        }
        {
            var Q0;
            Q0=qCreatedBy(id+"F36.planeOp",FACE);
            var sketch = newSketch(context, id + "F37", { "sketchPlane" : qUnion([Q0])});
            skCircle(sketch, "E102", {"center": v(31.33, -30.96) * mm, "radius": 9.53 * mm});
            skSolve(sketch);
        }
        {
            var Q0;
            Q0=sQuery(id+"F14.wireOp",VERTEX,"E95.2.internal");
            var Q1;
            Q1=sQuery(id+"F14.wireOp",EDGE,"E95");
            cPlane(context, id + "F38", {"entities" : qUnion([Q0, Q1]), "cplaneType" : CPlaneType.CURVE_POINT, "offset" : 25.4 * mm, "width" : 152.4 * mm, "height" : 152.4 * mm});
        }
        {
            var Q0;
            Q0=sQuery(id+"F14.wireOp",VERTEX,"E95.3.internal");
            var Q1;
            Q1=sQuery(id+"F14.wireOp",EDGE,"E95");
            cPlane(context, id + "F39", {"entities" : qUnion([Q0, Q1]), "cplaneType" : CPlaneType.CURVE_POINT, "offset" : 25.4 * mm, "width" : 152.4 * mm, "height" : 152.4 * mm});
        }
        {
            var Q0;
            Q0=sQuery(id+"F14.wireOp",VERTEX,"E95.4.internal");
            var Q1;
            Q1=sQuery(id+"F14.wireOp",EDGE,"E95");
            cPlane(context, id + "F40", {"entities" : qUnion([Q0, Q1]), "cplaneType" : CPlaneType.CURVE_POINT, "offset" : 25.4 * mm, "width" : 152.4 * mm, "height" : 152.4 * mm});
        }
        {
            var Q0;
            Q0=qCreatedBy(id+"F40.planeOp",FACE);
            var sketch = newSketch(context, id + "F41", { "sketchPlane" : qUnion([Q0])});
            skCircle(sketch, "E103", {"center": v(45.1, 53.2) * mm, "radius": 9.53 * mm});
            skSolve(sketch);
        }
        {
            var Q0;
            Q0=makeQuery(id+"F9.imprint","IMPRINT",FACE,{"disambiguationData":[TD([[makeQuery(id+"F9.imprint","IMPRINT",EDGE,{"derivedFrom":sQuery(id+"F9.wireOp",EDGE,"E82")}),1.0]])]});
            var Q1;
            Q1=sQuery(id+"F11.wireOp",EDGE,"E91");
            sweep(context, id + "F42", {"profiles" : qUnion([Q0]), "path" : qUnion([Q1])});
        }
        {
            var Q0;
            Q0=makeQuery(id+"F37.imprint","IMPRINT",FACE,{"disambiguationData":[TD([[makeQuery(id+"F37.imprint","IMPRINT",EDGE,{"derivedFrom":sQuery(id+"F37.wireOp",EDGE,"E102")}),1.0]])]});
            var Q1;
            Q1=sQuery(id+"F12.wireOp",EDGE,"E92");
            sweep(context, id + "F43", {"operationType" : NewBodyOperationType.ADD, "profiles" : qUnion([Q0]), "path" : qUnion([Q1])});
        }
        {
            var Q0;
            Q0=makeQuery(id+"F41.imprint","IMPRINT",FACE,{"disambiguationData":[TD([[makeQuery(id+"F41.imprint","IMPRINT",EDGE,{"derivedFrom":sQuery(id+"F41.wireOp",EDGE,"E103")}),1.0]])]});
            var Q1;
            Q1=sQuery(id+"F14.wireOp",EDGE,"E95");
            sweep(context, id + "F44", {"operationType" : NewBodyOperationType.ADD, "profiles" : qUnion([Q0]), "path" : qUnion([Q1])});
        }
        {
            var Q0;
            Q0=makeQuery(id+"F44.opSweep","CAP_FACE",FACE,{"disambiguationData":[OSD([sQuery(id+"F14.wireOp",VERTEX,"E95.end"),sQuery(id+"F41.wireOp",EDGE,"E103")])],"isStart":true});
            var Q1;
            Q1=makeQuery(id+"F25.opLoft","CAP_FACE",FACE,{"disambiguationData":[OSD([makeQuery(id+"F22.imprint","IMPRINT",FACE,{"disambiguationData":[TD([[makeQuery(id+"F22.imprint","IMPRINT",EDGE,{"derivedFrom":sQuery(id+"F22.wireOp",EDGE,"E100")}),1.0]])]})])],"isStart":true});
            loft(context, id + "F45", {"sheetProfilesArray" : [{ "sheetProfileEntities" : qUnion([Q0]) }, { "sheetProfileEntities" : qUnion([Q1]) }]});
        }
    });
